# Revit family: 638-00-116-DN80-300
name_source: partatom
category: Pipe Accessories
units: mm (PartAtom-declared; Revit-internal decimal feet)

## family parameters
Always vertical = No
Cut with Voids When Loaded = No
Part Type = Valve - Breaks Into
Round Connector Dimension = Use Diameter
Shared = No
Work Plane-Based = No

## types (7) — shared parameters
Body_Wallthickness = 15 mm  [stored 0.0492126 ft]
DN080_PN16 = 638-090-00-066416099
DN100_PN16 = 638-110-00-066416099
DN125_PN16 = 638-125-00-066416099
DN150_PN16 = 638-160-00-066416099
DN200_PN16 = 638-200-00-066416099
DN250_PN16 = 638-250-00-0664160
DN300_PN16 = 638-315-00-0664160
Description_ = AVK GATE VALVE, SUPA MAXI™, PE PIPE ENDS
Ftc = 4 mm  [stored 0.0131234 ft]
Name_Height_reference = 10 mm  [stored 0.0328084 ft]
Rib_Thickness = 18 mm  [stored 0.0590551 ft]
Search_table = 638-00-116-DN80-300
URL product pages = https://www.avkvalves.com
zero-valued in all types: Bottom_Reference

## per-type parameters (varying)
- DN080_PN16: At=70 mm; Body_Height=108 mm; Body_depth=140 mm; Body_width=75 mm; Bonnet_Flange_Depth=171 mm; Bonnet_Flange_Width=76 mm; Bonnet_Flange_cut=8 mm  [stored 0.0262467 ft]; Bonnet_Flange_thickness=15 mm  [stored 0.0492126 ft]; Bonnet_Height=54 mm  [stored 0.177165 ft]; Bonnet_Reference_height=98 mm; Bonnet_Thickness=77 mm; Bt=77 mm; Bt_2=69 mm; CL _Thickness=27 mm  [stored 0.0885827 ft]; CL_Height=75 mm; Cut_Reference=910 mm; D=90 mm; D1=10 mm  [stored 0.0328084 ft]; D2=35 mm  [stored 0.114829 ft]; D_ref_2=74 mm; E=15 mm  [stored 0.0492126 ft]; F=9 mm; F1=20 mm  [stored 0.0656168 ft]; FOD_2=120 mm; FOD_2_L=46 mm  [stored 0.150919 ft]; Fillet_Thickness=6 mm  [stored 0.019685 ft]; Flange_OR=214 mm; Flange_OR_ref=178 mm; Flange_Thickness=19 mm  [stored 0.062336 ft]; Flange_Thickness_cut=34 mm  [stored 0.111549 ft]; Ftc_reference_height=214 mm; H=282 mm; H1=247 mm; H3=400 mm; Horizontal_Flange_width=236 mm; ID (Radius)=40 mm  [stored 0.131234 ft]; L=680 mm; L1=255 mm; L_Dia=80 mm; L_ref=303 mm; L_ref_2=182 mm; L_ref_3=455 mm; L_ref_4=228 mm; Name_Reference=90 mm; Name_Width=38 mm  [stored 0.124672 ft]; Neck_H=64 mm; Neck_T=25 mm  [stored 0.082021 ft]; Neck_T2=23 mm; Nominal Diameter (DN)=80 mm; R1tv=1070 mm; R2f=15 mm  [stored 0.0492126 ft]; RF_Dia=66 mm; Rf=393 mm; Rib_Height_Reference_1=120 mm; Rib_Height_Reference_2=110 mm; Rib_Height_Reference_3=100 mm; Rib_Height_Reference_4=85 mm; Rib_Width_1=38 mm  [stored 0.124672 ft]; Rib_Width_2=38 mm  [stored 0.124672 ft]; Rib_Width_3=38 mm  [stored 0.124672 ft]; Rib_depth_1=38 mm  [stored 0.124672 ft]; Rib_depth_2=38 mm  [stored 0.124672 ft]; Rib_depth_3=38 mm  [stored 0.124672 ft]; Rt=357 mm; SR=94 mm
- DN100_PN16: At=83 mm; Body_Height=122 mm; Body_depth=166 mm; Body_width=80 mm; Bonnet_Flange_Depth=192 mm; Bonnet_Flange_Width=81 mm; Bonnet_Flange_cut=8 mm  [stored 0.0262467 ft]; Bonnet_Flange_thickness=15 mm  [stored 0.0492126 ft]; Bonnet_Height=67 mm; Bonnet_Reference_height=112 mm; Bonnet_Thickness=82 mm; Bt=82 mm; Bt_2=74 mm; CL _Thickness=29 mm  [stored 0.0951444 ft]; CL_Height=88 mm; Cut_Reference=916 mm; D=110 mm; D1=10 mm  [stored 0.0328084 ft]; D2=34 mm  [stored 0.111549 ft]; D_ref_2=93 mm; E=15 mm  [stored 0.0492126 ft]; F=10 mm  [stored 0.0328084 ft]; F1=22 mm  [stored 0.0721785 ft]; FOD_2=145 mm; FOD_2_L=62 mm  [stored 0.203412 ft]; Fillet_Thickness=6 mm  [stored 0.019685 ft]; Flange_OR=267 mm; Flange_OR_ref=223 mm; Flange_Thickness=19 mm  [stored 0.062336 ft]; Flange_Thickness_cut=42 mm  [stored 0.137795 ft]; Ftc_reference_height=267 mm; H=305 mm; H1=271 mm; H3=430 mm; Horizontal_Flange_width=250 mm; ID (Radius)=50 mm  [stored 0.164042 ft]; L=680 mm; L1=250 mm; L_Dia=100 mm; L_ref=305 mm; L_ref_2=183 mm; L_ref_3=458 mm; L_ref_4=229 mm; Name_Reference=101 mm; Name_Width=40 mm  [stored 0.131234 ft]; Neck_H=61 mm  [stored 0.200131 ft]; Neck_T=27 mm  [stored 0.0885827 ft]; Neck_T2=25 mm  [stored 0.082021 ft]; Nominal Diameter (DN)=100 mm; R1tv=1335 mm; R2f=15 mm  [stored 0.0492126 ft]; RF_Dia=78 mm; Rf=417 mm; Rib_Height_Reference_1=120 mm; Rib_Height_Reference_2=110 mm; Rib_Height_Reference_3=100 mm; Rib_Height_Reference_4=90 mm; Rib_Width_1=40 mm  [stored 0.131234 ft]; Rib_Width_2=40 mm  [stored 0.131234 ft]; Rib_Width_3=40 mm  [stored 0.131234 ft]; Rib_depth_1=40 mm  [stored 0.131234 ft]; Rib_depth_2=40 mm  [stored 0.131234 ft]; Rib_depth_3=40 mm  [stored 0.131234 ft]; Rt=445 mm; SR=119 mm
- DN125_PN16: At=97 mm; Body_Height=137 mm; Body_depth=194 mm; Body_width=90 mm; Bonnet_Flange_Depth=220 mm; Bonnet_Flange_Width=83 mm; Bonnet_Flange_cut=8 mm  [stored 0.0262467 ft]; Bonnet_Flange_thickness=15 mm  [stored 0.0492126 ft]; Bonnet_Height=66 mm; Bonnet_Reference_height=127 mm; Bonnet_Thickness=92 mm; Bt=92 mm; Bt_2=84 mm; CL _Thickness=34 mm  [stored 0.111549 ft]; CL_Height=102 mm; Cut_Reference=902 mm; D=125 mm; D1=10 mm  [stored 0.0328084 ft]; D2=34 mm  [stored 0.111549 ft]; D_ref_2=91 mm; E=15 mm  [stored 0.0492126 ft]; F=10 mm  [stored 0.0328084 ft]; F1=22 mm  [stored 0.0721785 ft]; FOD_2=162 mm; FOD_2_L=61 mm  [stored 0.200131 ft]; Fillet_Thickness=6 mm  [stored 0.019685 ft]; Flange_OR=263 mm; Flange_OR_ref=219 mm; Flange_Thickness=19 mm  [stored 0.062336 ft]; Flange_Thickness_cut=35 mm  [stored 0.114829 ft]; Ftc_reference_height=263 mm; H=346 mm; H1=312 mm; H3=467 mm; Horizontal_Flange_width=242 mm; ID (Radius)=63 mm  [stored 0.206693 ft]; L=662 mm; L1=250 mm; L_Dia=125 mm; L_ref=301 mm; L_ref_2=180 mm; L_ref_3=451 mm; L_ref_4=226 mm; Name_Reference=114 mm; Name_Width=45 mm  [stored 0.147638 ft]; Neck_H=73 mm; Neck_T=32 mm  [stored 0.104987 ft]; Neck_T2=30 mm  [stored 0.0984252 ft]; Nominal Diameter (DN)=125 mm; R1tv=1315 mm; R2f=15 mm  [stored 0.0492126 ft]; RF_Dia=92 mm; Rf=403 mm; Rib_Height_Reference_1=120 mm; Rib_Height_Reference_2=110 mm; Rib_Height_Reference_3=100 mm; Rib_Height_Reference_4=120 mm; Rib_Width_1=45 mm  [stored 0.147638 ft]; Rib_Width_2=45 mm  [stored 0.147638 ft]; Rib_Width_3=45 mm  [stored 0.147638 ft]; Rib_depth_1=45 mm  [stored 0.147638 ft]; Rib_depth_2=45 mm  [stored 0.147638 ft]; Rib_depth_3=45 mm  [stored 0.147638 ft]; Rt=438 mm; SR=119 mm
- DN150_PN16: At=121 mm; Body_Height=172 mm; Body_depth=242 mm; Body_width=95 mm; Bonnet_Flange_Depth=272 mm; Bonnet_Flange_Width=116 mm; Bonnet_Flange_cut=8 mm  [stored 0.0262467 ft]; Bonnet_Flange_thickness=15 mm  [stored 0.0492126 ft]; Bonnet_Height=85 mm; Bonnet_Reference_height=162 mm; Bonnet_Thickness=97 mm; Bt=97 mm; Bt_2=89 mm; CL _Thickness=34 mm  [stored 0.111549 ft]; CL_Height=126 mm; Cut_Reference=998 mm; D=160 mm; D1=10 mm  [stored 0.0328084 ft]; D2=34 mm  [stored 0.111549 ft]; D_ref_2=118 mm; E=15 mm  [stored 0.0492126 ft]; F=10 mm  [stored 0.0328084 ft]; F1=22 mm  [stored 0.0721785 ft]; FOD_2=202 mm; FOD_2_L=80 mm; Fillet_Thickness=12 mm  [stored 0.0393701 ft]; Flange_OR=339 mm; Flange_OR_ref=283 mm; Flange_Thickness=19 mm  [stored 0.062336 ft]; Flange_Thickness_cut=47 mm  [stored 0.154199 ft]; Ftc_reference_height=339 mm; H=400 mm; H1=366 mm; H3=557 mm; Horizontal_Flange_width=314 mm; ID (Radius)=75 mm; L=769 mm; L1=325 mm; L_Dia=150 mm; L_ref=333 mm; L_ref_2=200 mm; L_ref_3=499 mm; L_ref_4=250 mm; Name_Reference=143 mm; Name_Width=48 mm  [stored 0.15748 ft]; Neck_H=68 mm; Neck_T=32 mm  [stored 0.104987 ft]; Neck_T2=30 mm  [stored 0.0984252 ft]; Nominal Diameter (DN)=150 mm; R1tv=1695 mm; R2f=30 mm  [stored 0.0984252 ft]; RF_Dia=106 mm; Rf=523 mm; Rib_Height_Reference_1=120 mm; Rib_Height_Reference_2=110 mm; Rib_Height_Reference_3=100 mm; Rib_Height_Reference_4=150 mm; Rib_Width_1=48 mm  [stored 0.15748 ft]; Rib_Width_2=48 mm  [stored 0.15748 ft]; Rib_Width_3=48 mm  [stored 0.15748 ft]; Rib_depth_1=48 mm  [stored 0.15748 ft]; Rib_depth_2=48 mm  [stored 0.15748 ft]; Rib_depth_3=48 mm  [stored 0.15748 ft]; Rt=565 mm; SR=174 mm
- DN200_PN16: At=147 mm; Body_Height=220 mm; Body_depth=294 mm; Body_width=108 mm; Bonnet_Flange_Depth=332 mm; Bonnet_Flange_Width=132 mm; Bonnet_Flange_cut=13 mm; Bonnet_Flange_thickness=25 mm  [stored 0.082021 ft]; Bonnet_Height=97 mm; Bonnet_Reference_height=210 mm; Bonnet_Thickness=110 mm; Bt=110 mm; Bt_2=102 mm; CL _Thickness=34 mm  [stored 0.111549 ft]; CL_Height=152 mm; Cut_Reference=1098 mm; D=200 mm; D1=10 mm  [stored 0.0328084 ft]; D2=34 mm  [stored 0.111549 ft]; D_ref_2=135 mm; E=15 mm  [stored 0.0492126 ft]; F=12 mm  [stored 0.0393701 ft]; F1=27 mm  [stored 0.0885827 ft]; FOD_2=245 mm; FOD_2_L=104 mm; Fillet_Thickness=24 mm  [stored 0.0787402 ft]; Flange_OR=389 mm; Flange_OR_ref=324 mm; Flange_Thickness=20 mm  [stored 0.0656168 ft]; Flange_Thickness_cut=47 mm  [stored 0.154199 ft]; Ftc_reference_height=389 mm; H=490 mm; H1=456 mm; H3=672 mm; Horizontal_Flange_width=364 mm; ID (Radius)=100 mm; L=811 mm; L1=255 mm; L_Dia=200 mm; L_ref=366 mm; L_ref_2=220 mm; L_ref_3=549 mm; L_ref_4=275 mm; Name_Reference=183 mm; Name_Width=54 mm  [stored 0.177165 ft]; Neck_H=84 mm; Neck_T=32 mm  [stored 0.104987 ft]; Neck_T2=30 mm  [stored 0.0984252 ft]; Nominal Diameter (DN)=200 mm; R1tv=1945 mm; R2f=60 mm  [stored 0.19685 ft]; RF_Dia=133 mm; Rf=607 mm; Rib_Height_Reference_1=120 mm; Rib_Height_Reference_2=110 mm; Rib_Height_Reference_3=100 mm; Rib_Height_Reference_4=180 mm; Rib_Width_1=54 mm  [stored 0.177165 ft]; Rib_Width_2=54 mm  [stored 0.177165 ft]; Rib_Width_3=54 mm  [stored 0.177165 ft]; Rib_depth_1=54 mm  [stored 0.177165 ft]; Rib_depth_2=54 mm  [stored 0.177165 ft]; Rib_depth_3=54 mm  [stored 0.177165 ft]; Rt=648 mm; SR=210 mm
- DN250_PN16: At=171 mm; Body_Height=305 mm; Body_depth=342 mm; Body_width=124 mm; Bonnet_Flange_Depth=372 mm; Bonnet_Flange_Width=158 mm; Bonnet_Flange_cut=13 mm; Bonnet_Flange_thickness=25 mm  [stored 0.082021 ft]; Bonnet_Height=117 mm; Bonnet_Reference_height=295 mm; Bonnet_Thickness=126 mm; Bt=126 mm; Bt_2=118 mm; CL _Thickness=42 mm  [stored 0.137795 ft]; CL_Height=176 mm; Cut_Reference=1172 mm; D=250 mm; D1=15 mm  [stored 0.0492126 ft]; D2=47 mm  [stored 0.154199 ft]; D_ref_2=163 mm; E=13 mm; F=14 mm  [stored 0.0459318 ft]; F1=31 mm  [stored 0.101706 ft]; FOD_2=296 mm; FOD_2_L=136 mm; Fillet_Thickness=24 mm  [stored 0.0787402 ft]; Flange_OR=468 mm; Flange_OR_ref=390 mm; Flange_Thickness=22 mm  [stored 0.0721785 ft]; Flange_Thickness_cut=55 mm  [stored 0.180446 ft]; Ftc_reference_height=468 mm; H=664 mm; H1=617 mm; H3=886 mm; Horizontal_Flange_width=444 mm; ID (Radius)=125 mm; L=971 mm; L1=420 mm; L_Dia=250 mm; L_ref=391 mm; L_ref_2=234 mm; L_ref_3=586 mm; L_ref_4=293 mm; Name_Reference=270 mm; Name_Width=62 mm  [stored 0.203412 ft]; Neck_H=136 mm; Neck_T=40 mm  [stored 0.131234 ft]; Neck_T2=38 mm  [stored 0.124672 ft]; Nominal Diameter (DN)=250 mm; R1tv=2340 mm; R2f=60 mm  [stored 0.19685 ft]; RF_Dia=160 mm; Rf=740 mm; Rib_Height_Reference_1=90 mm; Rib_Height_Reference_2=110 mm; Rib_Height_Reference_3=100 mm; Rib_Height_Reference_4=200 mm; Rib_Width_1=140 mm; Rib_Width_2=140 mm; Rib_Width_3=62 mm  [stored 0.203412 ft]; Rib_depth_1=372 mm; Rib_depth_2=62 mm  [stored 0.203412 ft]; Rib_depth_3=62 mm  [stored 0.203412 ft]; Rt=780 mm; SR=284 mm
- DN300_PN16: At=209 mm; Body_Height=370 mm; Body_depth=418 mm; Body_width=157 mm; Bonnet_Flange_Depth=432 mm; Bonnet_Flange_Width=206 mm; Bonnet_Flange_cut=18 mm  [stored 0.0590551 ft]; Bonnet_Flange_thickness=35 mm  [stored 0.114829 ft]; Bonnet_Height=136 mm; Bonnet_Reference_height=360 mm; Bonnet_Thickness=160 mm; Bt=160 mm; Bt_2=151 mm; CL _Thickness=59 mm  [stored 0.19357 ft]; CL_Height=214 mm; Cut_Reference=1318 mm; D=315 mm; D1=15 mm  [stored 0.0492126 ft]; D2=47 mm  [stored 0.154199 ft]; D_ref_2=189 mm; E=13 mm; F=14 mm  [stored 0.0459318 ft]; F1=31 mm  [stored 0.101706 ft]; FOD_2=382 mm; FOD_2_L=143 mm; Fillet_Thickness=24 mm  [stored 0.0787402 ft]; Flange_OR=545 mm; Flange_OR_ref=454 mm; Flange_Thickness=25 mm  [stored 0.082021 ft]; Flange_Thickness_cut=61 mm  [stored 0.200131 ft]; Ftc_reference_height=545 mm; H=740 mm; H1=693 mm; H3=997 mm; Horizontal_Flange_width=514 mm; ID (Radius)=150 mm; L=1029 mm; L1=355 mm; L_Dia=300 mm; L_ref=439 mm; L_ref_2=264 mm; L_ref_3=659 mm; L_ref_4=330 mm; Name_Reference=250 mm; Name_Width=79 mm; Neck_H=109 mm; Neck_T=57 mm; Neck_T2=55 mm  [stored 0.180446 ft]; Nominal Diameter (DN)=300 mm; R1tv=2725 mm; R2f=60 mm  [stored 0.19685 ft]; RF_Dia=185 mm; Rf=857 mm; Rib_Height_Reference_1=178 mm; Rib_Height_Reference_2=285 mm; Rib_Height_Reference_3=150 mm; Rib_Height_Reference_4=300 mm; Rib_Width_1=180 mm; Rib_Width_2=180 mm; Rib_Width_3=79 mm; Rib_depth_1=432 mm; Rib_depth_2=432 mm; Rib_depth_3=79 mm; Rt=908 mm; SR=335 mm

note: [stored X ft] marks values corroborated as IEEE doubles in the binary element streams (Revit-internal decimal feet)

## geometry (parser evidence)
native form markers: Extrusion x1, Sweep x3
no freeform markers — native parametric forms only
